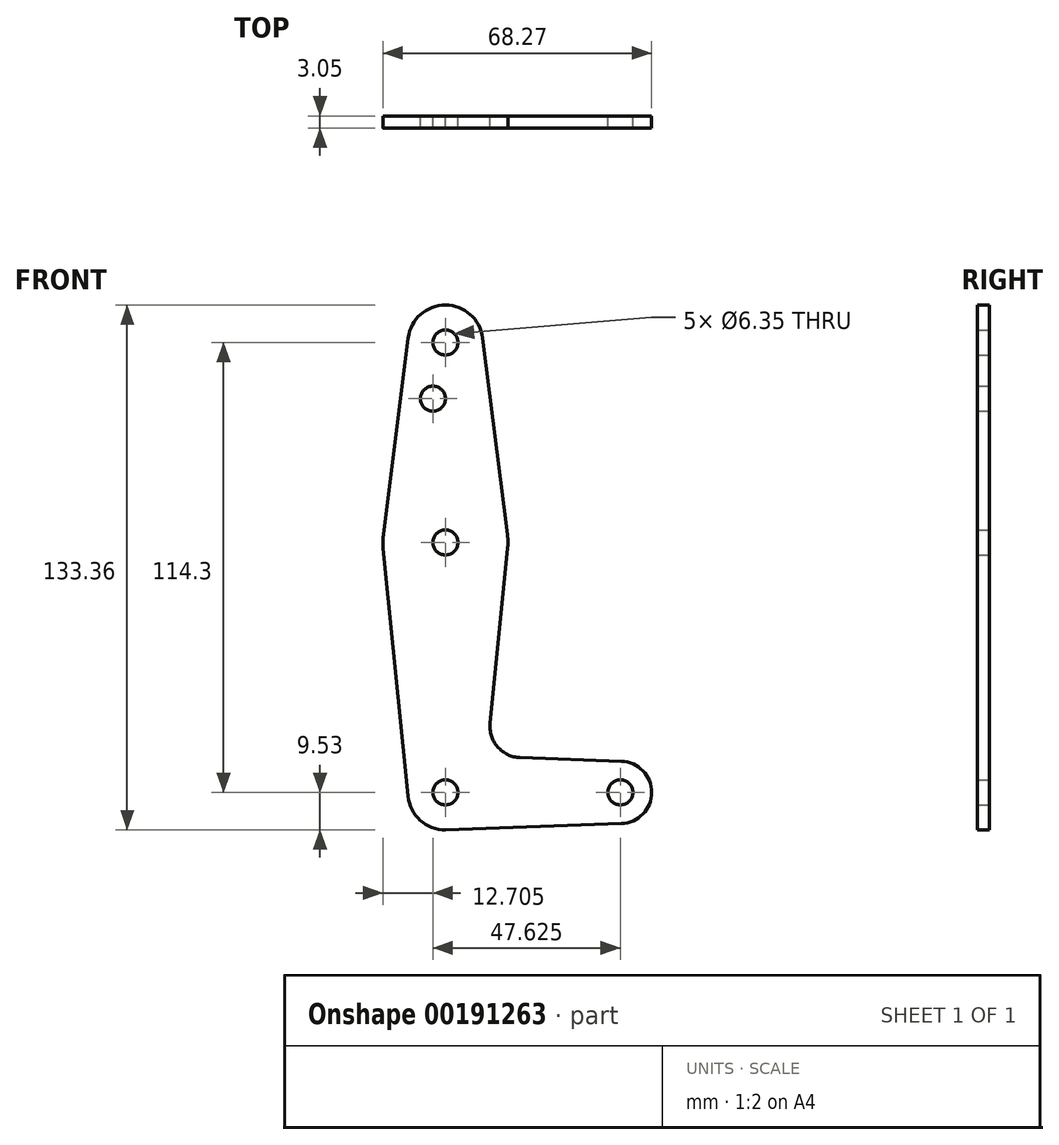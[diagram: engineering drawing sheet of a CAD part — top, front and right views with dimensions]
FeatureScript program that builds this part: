
annotation { "Feature Type Name" : "Feature", "Feature Type Description" : "" }
export const myFeature = defineFeature(function(context is Context, id is Id, definition is map)
    precondition{}
    {
        {
            var Q0;
            Q0=qCreatedBy(makeId("Front.planeOp"),FACE);
            var sketch = newSketch(context, id + "F0", { "sketchPlane" : qUnion([Q0])});
            skLineSegment(sketch, "E0", {"start": v(0, 0) * mm, "end": v(0, 63.5) * mm, "construction": true});
            skLineSegment(sketch, "E1", {"start": v(0, 63.5) * mm, "end": v(0, 114.3) * mm, "construction": true});
            skLineSegment(sketch, "E2", {"start": v(0, 0) * mm, "end": v(44.45, 0) * mm, "construction": true});
            skCircle(sketch, "E3", {"center": v(0, 114.3) * mm, "radius": 9.53 * mm});
            skCircle(sketch, "E4", {"center": v(0, 63.5) * mm, "radius": 15.88 * mm});
            skCircle(sketch, "E5", {"center": v(0, 0) * mm, "radius": 9.53 * mm});
            skCircle(sketch, "E6", {"center": v(44.45, 0) * mm, "radius": 7.94 * mm});
            skLineSegment(sketch, "E7", {"start": v(-9.45, 115.5) * mm, "end": v(-15.75, 65.48) * mm});
            skLineSegment(sketch, "E8", {"start": v(9.45, 115.5) * mm, "end": v(15.75, 65.48) * mm});
            skLineSegment(sketch, "E9", {"start": v(18.97, 8.85) * mm, "end": v(44.73, 7.93) * mm});
            skLineSegment(sketch, "E10", {"start": v(0, -9.52) * mm, "end": v(44.73, -7.93) * mm});
            skCircle(sketch, "E11", {"center": v(-3.18, 100.03) * mm, "radius": 3.18 * mm});
            skCircle(sketch, "E12", {"center": v(0, 63.5) * mm, "radius": 3.18 * mm});
            skCircle(sketch, "E13", {"center": v(0, 114.3) * mm, "radius": 3.18 * mm});
            skCircle(sketch, "E14", {"center": v(0, 0) * mm, "radius": 3.18 * mm});
            skCircle(sketch, "E15", {"center": v(44.45, 0) * mm, "radius": 3.18 * mm});
            skLineSegment(sketch, "E16", {"start": v(11.34, 17.59) * mm, "end": v(15.8, 61.91) * mm});
            skLineSegment(sketch, "E17", {"start": v(-15.8, 61.91) * mm, "end": v(-9.48, -0.95) * mm});
            skPoint(sketch, "E18.newPointB", {"position": v(0, 9.53) * mm});
            skArc(sketch, "E18.filletArc", {"start": v(11.34, 17.59) * mm, "mid": v(13.26, 11.57) * mm, "end": v(18.97, 8.85) * mm});
            skSolve(sketch);
        }
        {
            var Q0;
            {var subQ0=sQuery(id+"F0.wireOp",EDGE,"E9");Q0=makeQuery(id+"F0.imprint","IMPRINT",FACE,{"disambiguationData":[TD([[makeQuery(id+"F0.imprint","IMPRINT",EDGE,{"derivedFrom":subQ0}),-1.0]])]});}
            var Q1;
            {var subQ1=sQuery(id+"F0.wireOp",EDGE,"E7");Q1=makeQuery(id+"F0.imprint","IMPRINT",FACE,{"disambiguationData":[TD([[makeQuery(id+"F0.imprint","IMPRINT",EDGE,{"derivedFrom":subQ1}),1.0]])]});}
            var Q2;
            Q2=makeQuery(id+"F0.imprint","IMPRINT",FACE,{"disambiguationData":[TD([[makeQuery(id+"F0.imprint","IMPRINT",EDGE,{"derivedFrom":sQuery(id+"F0.wireOp",EDGE,"E12")}),-1.0]])]});
            var Q3;
            Q3=makeQuery(id+"F0.imprint","IMPRINT",FACE,{"disambiguationData":[TD([[makeQuery(id+"F0.imprint","IMPRINT",EDGE,{"derivedFrom":sQuery(id+"F0.wireOp",EDGE,"E13")}),-1.0]])]});
            var Q4;
            Q4=makeQuery(id+"F0.imprint","IMPRINT",FACE,{"disambiguationData":[TD([[makeQuery(id+"F0.imprint","IMPRINT",EDGE,{"derivedFrom":sQuery(id+"F0.wireOp",EDGE,"E14")}),-1.0]])]});
            var Q5;
            {var subQ0=sQuery(id+"F0.wireOp",EDGE,"E10");var subQ1=sQuery(id+"F0.wireOp",EDGE,"E5");var subQ2=makeQuery(id+"F0.imprint","INTERSECT",VERTEX,{"disambiguationData":[OD(0.0)],"derivedFrom":[subQ1,subQ0]});Q5=makeQuery(id+"F0.imprint","IMPRINT",FACE,{"disambiguationData":[TD([[makeQuery(id+"F0.imprint","IMPRINT",EDGE,{"disambiguationData":[TD([[subQ2,-1.0]])],"derivedFrom":subQ1}),1.0]])]});}
            var Q6;
            Q6=makeQuery(id+"F0.imprint","IMPRINT",FACE,{"disambiguationData":[TD([[makeQuery(id+"F0.imprint","IMPRINT",EDGE,{"derivedFrom":sQuery(id+"F0.wireOp",EDGE,"E15")}),-1.0]])]});
            extrude(context, id + "F1", {"entities" : qUnion([Q0, Q1, Q2, Q3, Q4, Q5, Q6]), "depth" : 3.05 * mm});
        }
    });
